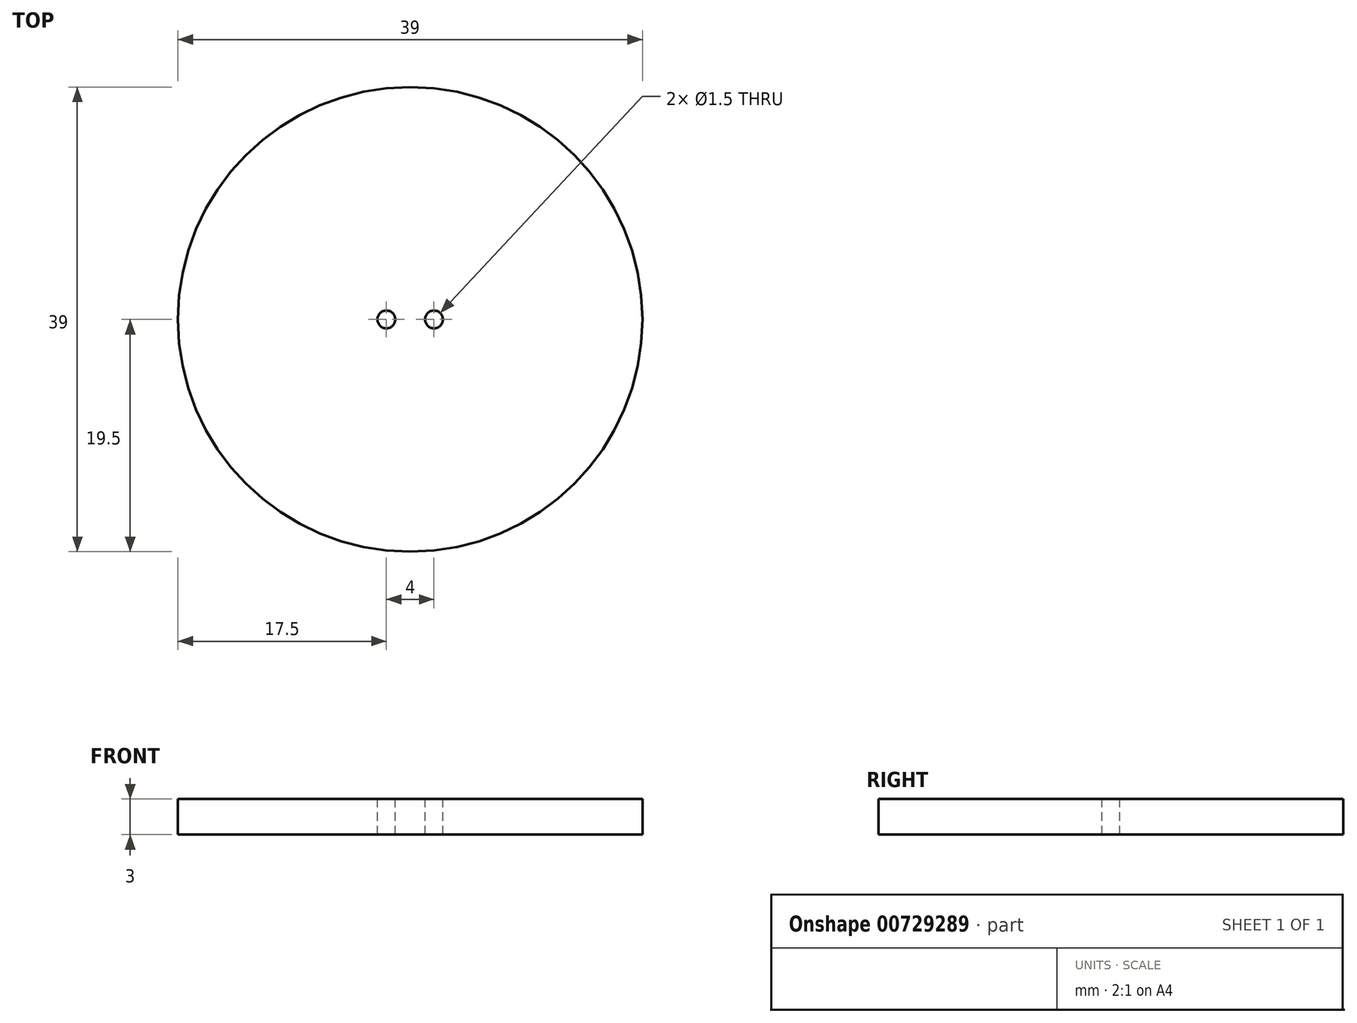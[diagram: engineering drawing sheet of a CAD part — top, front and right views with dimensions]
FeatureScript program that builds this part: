
annotation { "Feature Type Name" : "Feature", "Feature Type Description" : "" }
export const myFeature = defineFeature(function(context is Context, id is Id, definition is map)
    precondition{}
    {
        {
            var Q0;
            Q0=qCreatedBy(makeId("Top.planeOp"),FACE);
            var sketch = newSketch(context, id + "F0", { "sketchPlane" : qUnion([Q0])});
            skCircle(sketch, "E0", {"center": v(0, 0) * mm, "radius": 19.5 * mm});
            skSolve(sketch);
        }
        {
            var Q0;
            Q0 = qSketchRegion(id + "F0", true);
            extrude(context, id + "F1", {"entities" : qUnion([Q0]), "depth" : 3 * mm, "offsetDistance" : 25 * mm});
        }
        {
            var Q0;
            Q0=makeQuery(id+"F1.opExtrude","CAP_FACE",FACE,{"disambiguationData":[OSD([sQuery(id+"F0.wireOp",EDGE,"E0")])],"isStart":false});
            var sketch = newSketch(context, id + "F2", { "sketchPlane" : qUnion([Q0])});
            skCircle(sketch, "E1", {"center": v(2, 0) * mm, "radius": 0.75 * mm});
            skCircle(sketch, "E2.MirrorC", {"center": v(-2, 0) * mm, "radius": 0.75 * mm});
            skSolve(sketch);
        }
        {
            var Q0;
            Q0 = qSketchRegion(id + "F2", true);
            extrude(context, id + "F3", {"entities" : qUnion([Q0]), "operationType" : NewBodyOperationType.REMOVE, "oppositeDirection" : true, "depth" : 25 * mm, "offsetDistance" : 25 * mm});
        }
    });
